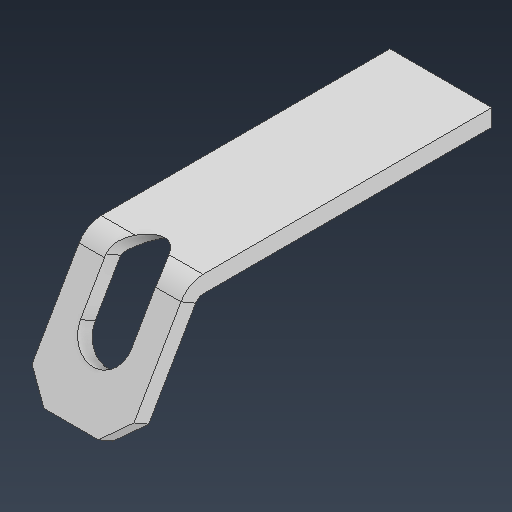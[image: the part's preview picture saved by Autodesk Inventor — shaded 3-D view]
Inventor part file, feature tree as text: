
AUTODESK INVENTOR PART (.ipt)
format: ipt  version: 2021 (Build 250183000, 183)  size: 100,352 bytes
history: native  units: in
note: dims shown in document units (in); Inventor stores cm internally (conversion verified against a paired STEP export)
features: chamfer x1
ambient origin geometry x8: Origin, YZ Plane, XZ Plane, XY Plane, X Axis, Y Axis, Z Axis, Center Point
bodies: Solid1 (feature_tree)
feature tree (1):
  chamfer  "Chamfer1"  [1 undecoded]
note: 1 required parameter value undecoded (feature->parameter linkage not recoverable at this tier; creation-order binding heuristic only, values carry confidence <= 0.55)
